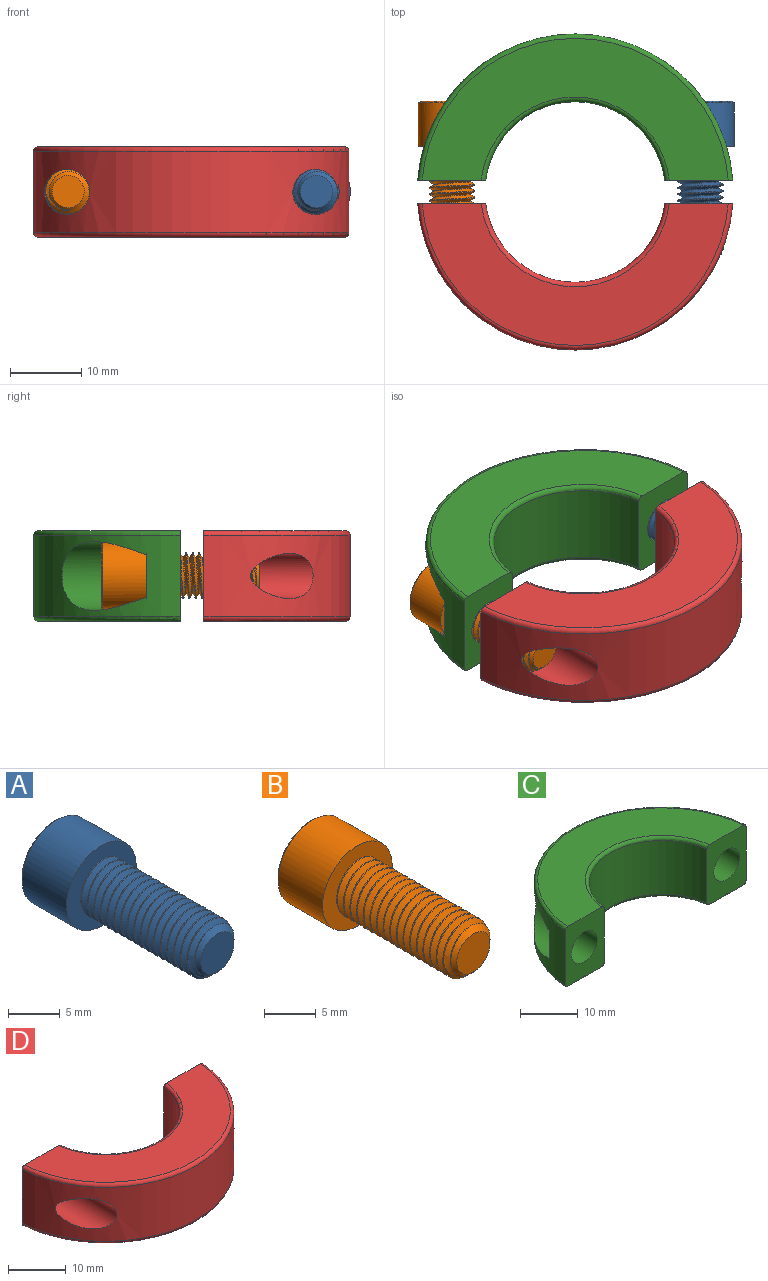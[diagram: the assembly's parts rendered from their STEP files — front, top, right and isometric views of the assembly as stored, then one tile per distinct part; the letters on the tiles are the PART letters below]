
ASSEMBLY  parts=4 mates=3
PART A: 17 faces, bbox 9.9x22.7x9.9 mm
  f0: cylinder r=3.17mm len=14.97mm, axis (0,-1,0), area 37.2mm2, adj f3,f13,f14,f15
  f1: plane 9.02x9.02mm, normal (0,1,0), area 44.2mm2, adj f5,f6,f7,f8,f9,f10,f12
  f2: cylinder r=4.76mm len=9.53mm, axis (0,-1,0), area 182.4mm2, adj f3,f12
  f3: plane 9.88x9.88mm, normal (0,-1,0), area 45.1mm2, adj f0,f2,f14,f15,f16
  f4: plane 4.54x4.54mm, normal (0,-1,0), area 16.2mm2, adj f13
  f5: plane 4.76x2.75mm, normal (0,0,-1), area 13.1mm2, adj f1,f6,f10,f11
  f6: plane 4.76x2.38mm, normal (0.87,0,-0.5), area 13.1mm2, adj f1,f5,f7,f11
  f7: plane 4.76x2.38mm, normal (0.87,0,0.5), area 13.1mm2, adj f1,f6,f8,f11
  f8: plane 4.76x2.75mm, normal (0,0,1), area 13.1mm2, adj f1,f7,f9,f11
  f9: plane 4.76x2.38mm, normal (-0.87,0,0.5), area 13.1mm2, adj f1,f8,f10,f11
  f10: plane 4.76x2.38mm, normal (-0.87,0,-0.5), area 13.1mm2, adj f1,f5,f9,f11
  f11: plane 5.5x4.76mm, normal (0,1,0), area 19.6mm2, adj f5,f6,f7,f8,f9,f10
  f12: cone r=4.76mm half-angle=45deg, axis (0,-1,0), area 10.5mm2, adj f1,f2
  f13: cone r=2.27mm half-angle=45deg, axis (0,1,0), area 14.2mm2, adj f0,f4,f14,f15,f16
  f14: bspline ~16.47x6.45mm, area 206.6mm2, adj f0,f3,f13,f16
  f15: bspline ~16.02x6.45mm, area 207.1mm2, adj f0,f3,f13,f16
  f16: cylinder r=2.59mm len=15.56mm, axis (0,-1,0), area 31.4mm2, adj f3,f13,f14,f15
PART B: 17 faces, bbox 9.9x22.7x9.9 mm
  f0: cylinder r=3.17mm len=14.97mm, axis (0,-1,0), area 37.2mm2, adj f3,f13,f14,f15
  f1: plane 9.02x9.02mm, normal (0,1,0), area 44.2mm2, adj f5,f6,f7,f8,f9,f10,f12
  f2: cylinder r=4.76mm len=9.53mm, axis (0,-1,0), area 182.4mm2, adj f3,f12
  f3: plane 9.88x9.88mm, normal (0,-1,0), area 45.1mm2, adj f0,f2,f14,f15,f16
  f4: plane 4.54x4.54mm, normal (0,-1,0), area 16.2mm2, adj f13
  f5: plane 4.76x2.75mm, normal (0,0,-1), area 13.1mm2, adj f1,f6,f10,f11
  f6: plane 4.76x2.38mm, normal (0.87,0,-0.5), area 13.1mm2, adj f1,f5,f7,f11
  f7: plane 4.76x2.38mm, normal (0.87,0,0.5), area 13.1mm2, adj f1,f6,f8,f11
  f8: plane 4.76x2.75mm, normal (0,0,1), area 13.1mm2, adj f1,f7,f9,f11
  f9: plane 4.76x2.38mm, normal (-0.87,0,0.5), area 13.1mm2, adj f1,f8,f10,f11
  f10: plane 4.76x2.38mm, normal (-0.87,0,-0.5), area 13.1mm2, adj f1,f5,f9,f11
  f11: plane 5.5x4.76mm, normal (0,1,0), area 19.6mm2, adj f5,f6,f7,f8,f9,f10
  f12: cone r=4.76mm half-angle=45deg, axis (0,-1,0), area 10.5mm2, adj f1,f2
  f13: cone r=2.27mm half-angle=45deg, axis (0,1,0), area 14.2mm2, adj f0,f4,f14,f15,f16
  f14: bspline ~16.47x6.45mm, area 206.6mm2, adj f0,f3,f13,f16
  f15: bspline ~16.02x6.45mm, area 207.1mm2, adj f0,f3,f13,f16
  f16: cylinder r=2.59mm len=15.56mm, axis (0,-1,0), area 31.4mm2, adj f3,f13,f14,f15
PART C: 18 faces, bbox 48x22.5x12.9 mm
  f0: plane 43.05x19.92mm, normal (0,0,-1), area 229.5mm2, adj f2,f4,f7,f11
  f1: cylinder r=22.23mm len=44.33mm, axis (0,0,-1), area 519.4mm2, adj f2,f4,f7,f8,f12,f13,f15,f16
  f2: plane 12.73x9.6mm, normal (0,-1,0), area 89.5mm2, adj f0,f1,f3,f5,f6,f7,f8,f9
  f3: cylinder r=12.7mm len=25.18mm, axis (0,0,-1), area 417.8mm2, adj f2,f4,f9,f10
  f4: plane 12.73x9.6mm, normal (0,-1,0), area 89.5mm2, adj f0,f1,f3,f5,f6,f7,f8,f9
  f5: plane 43.05x19.92mm, normal (0,0,1), area 425.3mm2, adj f2,f4,f8,f9
  f6: plane 34.38x15.61mm, normal (0,0,-1), area 176.1mm2, adj f2,f4,f10,f11
  f7: torus R=21.59mm, axis (0,0,1), area 65.6mm2, adj f0,f1,f2,f4
  f8: torus R=21.59mm, axis (0,0,1), area 65.6mm2, adj f1,f2,f4,f5
  f9: torus R=13.33mm, axis (0,0,1), area 37.2mm2, adj f2,f3,f4,f5
  f10: torus R=13.33mm, axis (0,0,1), area 37.2mm2, adj f2,f3,f4,f6
  f11: torus R=17.46mm, axis (0,0,-1), area 30.8mm2, adj f0,f2,f4,f6
  f12: plane 9.65x8.64mm, normal (0,1,0), area 37.4mm2, adj f1,f13,f14
  f13: cylinder r=4.83mm len=11.85mm, axis (0,-1,0), area 192.1mm2, adj f1,f12
  f14: cylinder r=3.17mm len=6.35mm, axis (0,-1,0), area 95mm2, adj f2,f12
  f15: cylinder r=4.83mm len=11.85mm, axis (0,-1,0), area 192.1mm2, adj f1,f16
  f16: plane 9.65x8.64mm, normal (0,1,0), area 37.4mm2, adj f1,f15,f17
  f17: cylinder r=3.17mm len=6.35mm, axis (0,-1,0), area 95mm2, adj f4,f16
PART D: 14 faces, bbox 48x22.5x12.9 mm
  f0: plane 43.05x19.92mm, normal (0,0,-1), area 229.5mm2, adj f2,f4,f10,f11
  f1: cylinder r=22.23mm len=44.33mm, axis (0,0,-1), area 652.6mm2, adj f2,f4,f7,f10,f12,f13
  f2: plane 12.73x9.6mm, normal (0,1,0), area 89.5mm2, adj f0,f1,f3,f5,f6,f7,f8,f9
  f3: cylinder r=12.7mm len=25.18mm, axis (0,0,-1), area 417.8mm2, adj f2,f4,f8,f9
  f4: plane 12.73x9.6mm, normal (0,1,0), area 89.5mm2, adj f0,f1,f3,f5,f6,f7,f8,f9
  f5: plane 43.05x19.92mm, normal (0,0,1), area 425.3mm2, adj f2,f4,f7,f8
  f6: plane 34.38x15.61mm, normal (0,0,-1), area 176.1mm2, adj f2,f4,f9,f11
  f7: torus R=21.59mm, axis (0,0,1), area 65.6mm2, adj f1,f2,f4,f5
  f8: torus R=13.33mm, axis (0,0,1), area 37.2mm2, adj f2,f3,f4,f5
  f9: torus R=13.33mm, axis (0,0,1), area 37.2mm2, adj f2,f3,f4,f6
  f10: torus R=21.59mm, axis (0,0,1), area 65.6mm2, adj f0,f1,f2,f4
  f11: torus R=17.46mm, axis (0,0,-1), area 30.8mm2, adj f0,f2,f4,f6
  f12: cylinder r=3.17mm len=15.36mm, axis (0,-1,0), area 230.3mm2, adj f1,f4
  f13: cylinder r=3.17mm len=15.36mm, axis (0,1,0), area 230.4mm2, adj f1,f2
PLACE A t=(0.16,0,0.07)mm
PLACE B t=(0.16,0,0.07)mm
PLACE C at identity
PLACE D at identity
MATE fastened C.f1 <-> D.f1  axis (0,0,1) through (0,0,6.35)mm
MATE fastened A.f3 <-> C.f15  axis (0,-1,0) through (17.46,6.43,0)mm
MATE fastened B.f3 <-> C.f13  axis (0,-1,0) through (-17.46,6.43,0)mm
